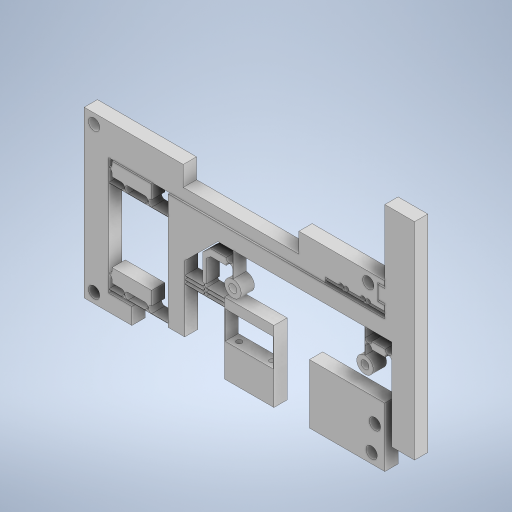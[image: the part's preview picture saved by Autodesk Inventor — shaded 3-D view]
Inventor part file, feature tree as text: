
AUTODESK INVENTOR PART (.ipt)
format: ipt  version: 2023 (Build 270158000, 158)  size: 700,928 bytes
history: native  units: mm
features: reference x11, extrude x9, sketch x8, other x6
ambient origin geometry x8: Origin, YZ Plane, XZ Plane, XY Plane, X Axis, Y Axis, Z Axis, Center Point
bodies: Solid1 (feature_tree)
feature tree (34):
  extrude  "Extrusion1"  Depth=20.0mm
  extrude  "Extrusion2"  Depth=4.0mm TaperAngle=0.0deg
  extrude  "Extrusion3"  Depth=0.5mm
  extrude  "Extrusion4"  Depth=5.0mm
  extrude  "Extrusion5"  Depth=18.0mm
  extrude  "Extrusion7"  Depth=1.0mm
  extrude  "Extrusion8"  Depth=1.0mm
  extrude  "Extrusion9"  Depth=0.1mm
  extrude  "Extrusion10"  Depth=5.0mm
  sketch  "Sketch1"  dims[d0=4.0mm d1=0.0mm d2=20.0mm]
  reference  "Reference1"
  sketch  "Sketch2"  dims[d3=9.0mm d4=4.0mm d5=0.0mm]
  sketch  "Sketch6"  dims[d6=7.0mm d7=0.5mm]
  reference  "Reference2"
  sketch  "Sketch7"  dims[d8=4.0mm d9=0.0mm d27=5.0mm]
  sketch  "Sketch9"  dims[d28=30.0mm d29=18.0mm]
  sketch  "Sketch10"  dims[d30=0.1mm d31=1.0mm]
  sketch  "Sketch11"  dims[d32=0.1mm d33=1.0mm]
  reference  "Reference3"
  reference  "Reference4"
  reference  "Reference5"
  reference  "Reference6"
  reference  "Reference7"
  reference  "Reference8"
  sketch  "Sketch12"  dims[d34=15.0mm d35=0.1mm d37=5.0mm d39=5.0mm d40=0.1mm d41=0.1mm d43=0.0mm d44=15.0mm d45=18.0mm d46=2.0mm d47=0.1mm d48=40.0mm d49=2.4mm d50=2.4mm d51=5.0mm d52=5.0mm d53=0.1mm d54=0.05mm d55=0.05mm d56=0.1mm d57=8.0mm d58=0.1mm d59=2.0mm d60=1.5mm d61=5.0mm d62=0.5mm d63=0.5mm d64=0.1mm d65=0.1mm d66=5.0mm d67=0.0mm d68=0.0mm d69=15.0mm d70=10.0mm d71=15.0mm d72=0.0mm d73=1.5mm d74=1.5mm d75=0.2mm d76=0.2mm d79=1.0mm d80=0.1mm d81=0.1mm d82=1.0mm d83=4.0mm d84=0.0mm d87=15.0mm d88=10.0mm d89=10.0mm d90=10.0mm d91=10.0mm d92=0.1mm d93=0.75mm d94=2.0mm d95=1.5mm d97=18.0mm d98=7.0mm d99=4.0mm d100=0.0mm d105=2.0mm d106=6.9mm d107=20.0mm d108=35.0mm d110=6.0mm d111=4.0mm d112=0.0mm d113=2.0mm d114=2.0mm d115=10.0mm d116=2.5mm d117=1.6mm d118=1.6mm d119=10.0mm d120=0.0mm d121=30.0mm d122=10.0mm d123=0.0mm d124=13.0mm d125=3.0mm d126=3.0mm d127=4.0mm d128=3.4mm d129=3.4mm d130=0.1mm d131=7.0mm d132=5.0mm d133=8.0mm d134=0.0mm d135=12.0mm d140=-1.0mm d141=1.0mm d142=2.0mm d143=2.0mm d144=2.1mm d145=2.0mm d146=2.0mm d147=2.1mm d148=0.0mm d149=1.0mm d150=1.0mm d151=2.0mm d152=2.0mm d153=5.0mm d154=1.6mm d155=5.0mm d156=1.6mm d157=1.0mm d158=1.0mm d159=1.0mm d160=1.0mm d161=1.1mm d162=1.1mm d163=5.45mm d164=5.45mm d165=1.0mm d166=1.0mm d167=5.0mm d168=2.0mm d169=2.1mm d170=2.0mm d171=5.0mm d172=2.1mm d173=2.0mm d174=2.0mm d176=2.0mm d177=2.0mm d178=2.1mm d179=2.0mm d180=2.0mm d181=5.0mm d182=2.1mm d183=5.0mm d184=2.1mm d185=2.0mm d186=2.0mm d187=2.0mm d188=2.0mm d189=2.1mm d190=2.1mm d191=2.9mm d192=2.9mm d193=1.1mm d194=0.0mm d24=0.5mm d25=0.872665mm d26=0.5mm]
  reference  "Reference9"
  reference  "Reference10"
  reference  "Reference11"
  other  "<userpath>\ClawdDrive\Objet3D\IminaProbe\V3Roue\RoueV3.iam"
  other  "RoueV3.iam"
  other  "RoueV3partA:1"
  other  "DifferentialLinearActuator:1"
  other  "RoueV3PartC:1"
  other  "DifferentialLinearActuator:5"
